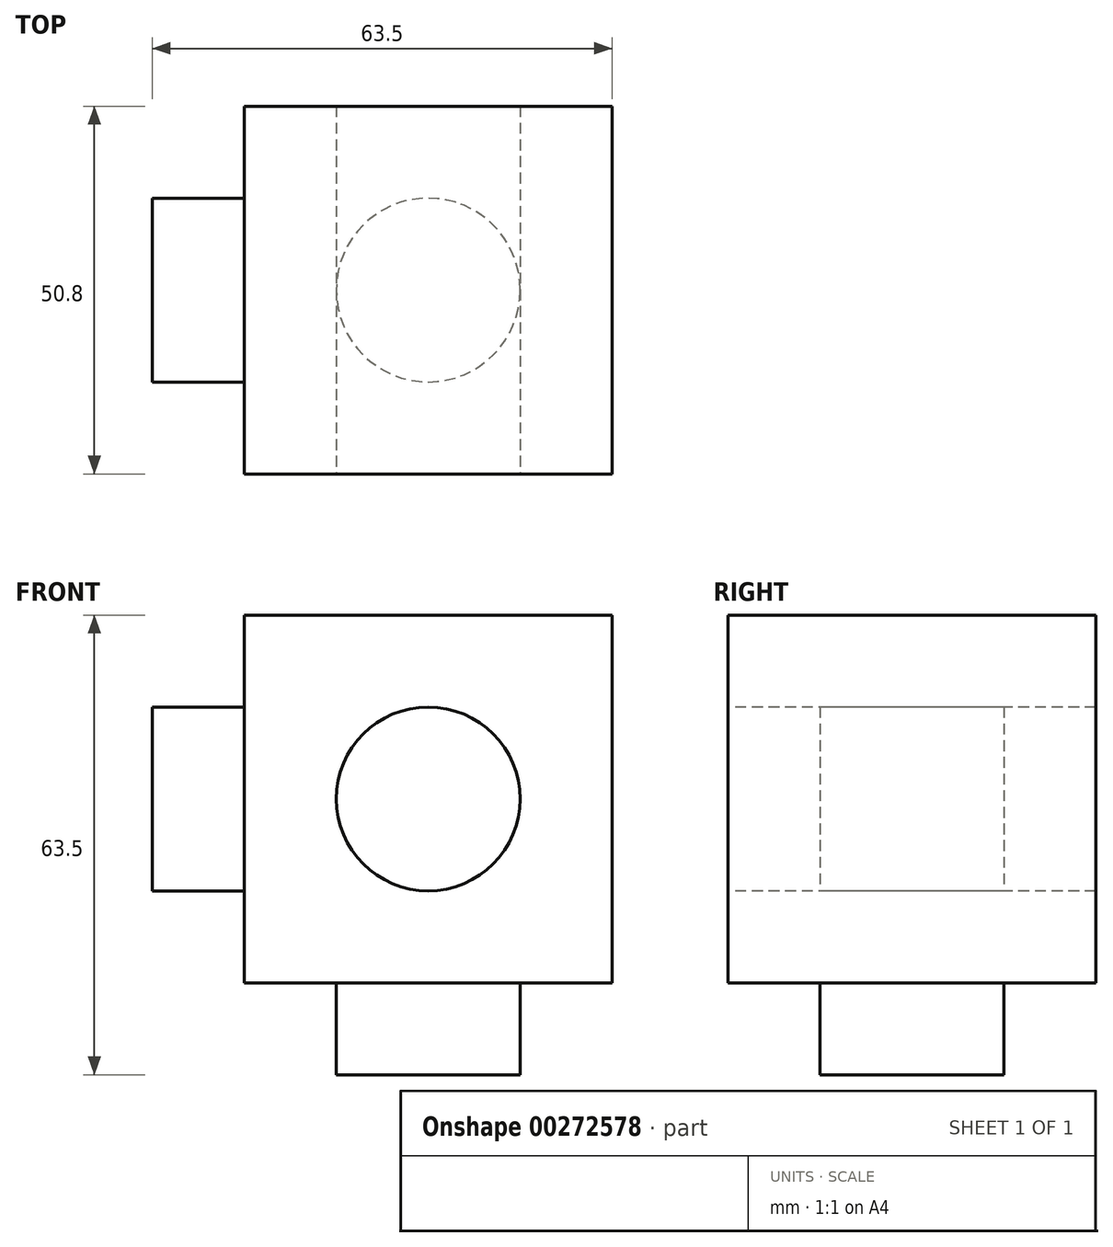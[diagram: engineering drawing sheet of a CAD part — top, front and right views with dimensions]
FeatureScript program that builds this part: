
annotation { "Feature Type Name" : "Feature", "Feature Type Description" : "" }
export const myFeature = defineFeature(function(context is Context, id is Id, definition is map)
    precondition{}
    {
        {
            var Q0;
            Q0=qCreatedBy(makeId("Front.planeOp"),FACE);
            var sketch = newSketch(context, id + "F0", { "sketchPlane" : qUnion([Q0])});
            skLineSegment(sketch, "E0.bottom", {"start": v(0, 0) * mm, "end": v(-50.8, 0) * mm});
            skLineSegment(sketch, "E0.top", {"start": v(0, 50.8) * mm, "end": v(-50.8, 50.8) * mm});
            skLineSegment(sketch, "E0.left", {"start": v(0, 0) * mm, "end": v(0, 50.8) * mm});
            skLineSegment(sketch, "E0.right", {"start": v(-50.8, 0) * mm, "end": v(-50.8, 50.8) * mm});
            skSolve(sketch);
        }
        {
            var Q0;
            Q0 = qSketchRegion(id + "F0", true);
            extrude(context, id + "F1", {"entities" : qUnion([Q0]), "depth" : 50.8 * mm});
        }
        {
            var Q0;
            Q0=makeQuery(id+"F1.opExtrude","CAP_FACE",FACE,{"disambiguationData":[OSD([sQuery(id+"F0.wireOp",EDGE,"E0.bottom"),sQuery(id+"F0.wireOp",EDGE,"E0.top"),sQuery(id+"F0.wireOp",EDGE,"E0.left"),sQuery(id+"F0.wireOp",EDGE,"E0.right")])],"isStart":false});
            var sketch = newSketch(context, id + "F2", { "sketchPlane" : qUnion([Q0])});
            skCircle(sketch, "E1", {"center": v(-25.4, 25.4) * mm, "radius": 12.7 * mm});
            skSolve(sketch);
        }
        {
            var Q0;
            Q0 = qSketchRegion(id + "F2", true);
            extrude(context, id + "F3", {"entities" : qUnion([Q0]), "operationType" : NewBodyOperationType.REMOVE, "oppositeDirection" : true, "depth" : 50.8 * mm});
        }
        {
            var Q0;
            Q0=makeQuery(id+"F1.opExtrude","SWEPT_FACE",FACE,{"disambiguationData":[OSD([sQuery(id+"F0.wireOp",EDGE,"E0.right")])]});
            var sketch = newSketch(context, id + "F4", { "sketchPlane" : qUnion([Q0])});
            skLineSegment(sketch, "E2.bottom", {"start": v(12.7, 38.1) * mm, "end": v(38.1, 38.1) * mm});
            skLineSegment(sketch, "E2.top", {"start": v(12.7, 12.7) * mm, "end": v(38.1, 12.7) * mm});
            skLineSegment(sketch, "E2.left", {"start": v(12.7, 38.1) * mm, "end": v(12.7, 12.7) * mm});
            skLineSegment(sketch, "E2.right", {"start": v(38.1, 38.1) * mm, "end": v(38.1, 12.7) * mm});
            skSolve(sketch);
        }
        {
            var Q0;
            Q0 = qSketchRegion(id + "F4", true);
            extrude(context, id + "F5", {"entities" : qUnion([Q0]), "operationType" : NewBodyOperationType.ADD, "depth" : 12.7 * mm});
        }
        {
            var Q0;
            Q0=makeQuery(id+"F1.opExtrude","SWEPT_FACE",FACE,{"disambiguationData":[OSD([sQuery(id+"F0.wireOp",EDGE,"E0.bottom")])]});
            var sketch = newSketch(context, id + "F6", { "sketchPlane" : qUnion([Q0])});
            skCircle(sketch, "E3", {"center": v(-25.4, 25.4) * mm, "radius": 12.7 * mm});
            skSolve(sketch);
        }
        {
            var Q0;
            Q0 = qSketchRegion(id + "F6", true);
            extrude(context, id + "F7", {"entities" : qUnion([Q0]), "operationType" : NewBodyOperationType.ADD, "depth" : 12.7 * mm});
        }
    });
